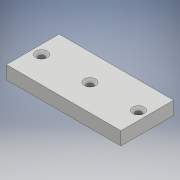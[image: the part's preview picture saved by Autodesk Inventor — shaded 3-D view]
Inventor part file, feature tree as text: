
AUTODESK INVENTOR PART (.ipt)
format: ipt  version: 2018 (Build 220112000, 112)  size: 104,960 bytes
history: native  units: mm
features: extrude x1, chamfer x1, sketch x1
ambient origin geometry x8: Origin, YZ Plane, XZ Plane, XY Plane, X Axis, Y Axis, Z Axis, Center Point
bodies: Solid1 (feature_tree)
feature tree (3):
  extrude  "Extrusion1"  Depth=30.0mm
  chamfer  "Chamfer1"  Distance=3.5mm
  sketch  "Sketch1"  dims[d0=65.0mm d1=30.0mm d2=3.5mm d3=5.0mm d4=5.0mm d5=7.5mm d6=0.0mm d7=1.5mm d8=2.0mm d9=45.0deg]
